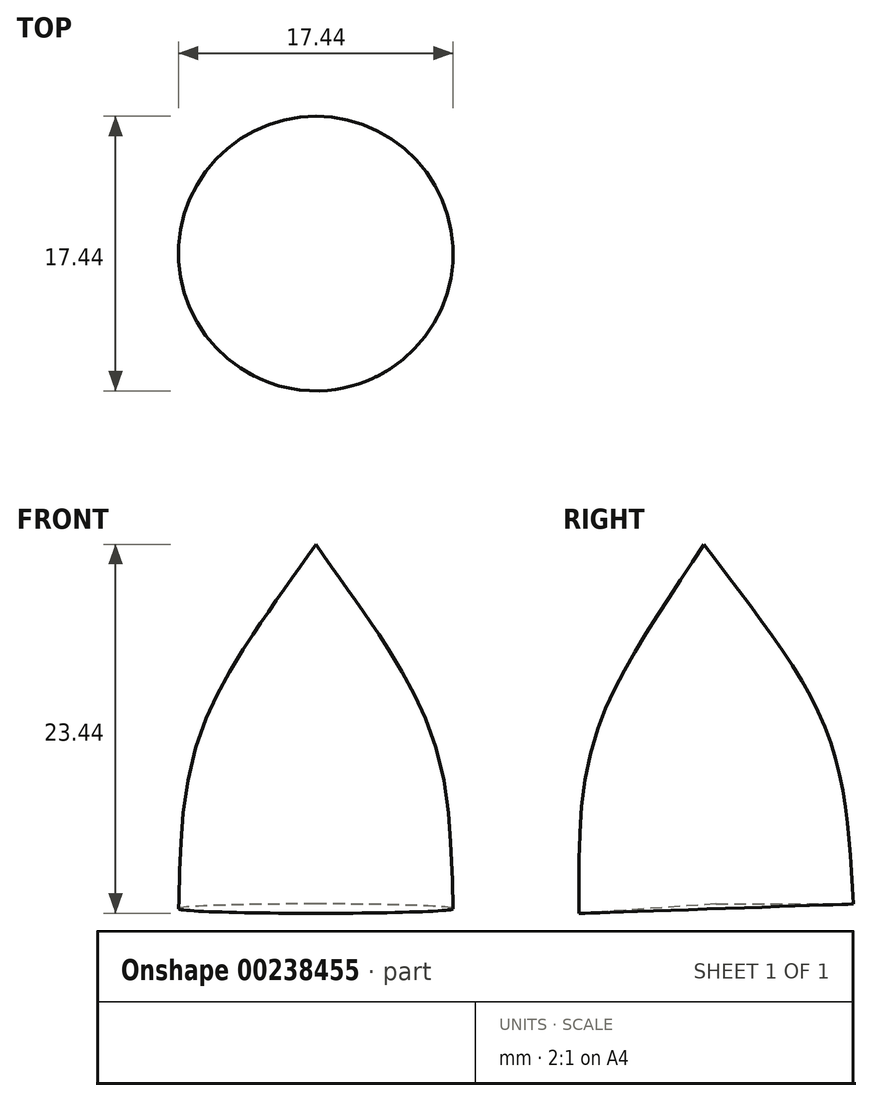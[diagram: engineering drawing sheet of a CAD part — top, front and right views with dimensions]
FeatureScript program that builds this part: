
annotation { "Feature Type Name" : "Feature", "Feature Type Description" : "" }
export const myFeature = defineFeature(function(context is Context, id is Id, definition is map)
    precondition{}
    {
        {
            var Q0;
            Q0=qCreatedBy(makeId("Right.planeOp"),FACE);
            var sketch = newSketch(context, id + "F0", { "sketchPlane" : qUnion([Q0])});
            skFitSpline(sketch, "E0", {"points": [v(28.67, 2.03) * mm, v(36.41, -9.73) * mm, v(38.18, -20.82) * mm], "startDerivative": vector(16.6, -22.46) * mm, "endDerivative": vector(1.61, -23.62) * mm});
            skLineSegment(sketch, "E1", {"start": v(29.45, -20.82) * mm, "end": v(38.18, -20.82) * mm});
            skLineSegment(sketch, "E2", {"start": v(28.67, 2.03) * mm, "end": v(29.45, -20.82) * mm});
            skSolve(sketch);
        }
        {
            var Q0;
            Q0 = qSketchRegion(id + "F0", true);
            var Q1;
            Q1=sQuery(id+"F0.wireOp",EDGE,"E2");
            revolve(context, id + "F1", {"entities" : qUnion([Q0]), "axis" : qUnion([Q1]), "revolveType" : RevolveType.FULL});
        }
    });
